# Revit family: Electronics_Amplifiers_Biamp_Tesira_4-Channel-PoE_AMP-450P__
name_source: partatom
category: Communication Devices
units: mm (PartAtom-declared; Revit-internal decimal feet)

## family parameters
Cut with Voids When Loaded = Yes
Host = Face
Maintain Annotation Orientation = No
OmniClass Number = 23.85.10.11.14.14.17
OmniClass Title = Sound Amplifiers
Part Type = Normal
Room Calculation Point = No
Round Connector Dimension = Use Diameter
Shared = No

## types (1)
- AMP-450P
    Altitude = 0-10,000 ft (0-3000m) MSL
    Amplifier Topology = Class D
    Apparent Load = 0 VA
    Burst Power Output = 4 ohm per channel: 50W per ANSI/CTA-2006-B at 1kHz; 8 ohm per channel: 30W per ANSI/CTA-2006-B at 1kHz
    Compliance = FCC Part 15B (USA); UL and C-UL listed (USA and Canada); CE Marked (Europe); KCC (Korea); RoHS Directive (Europe); Evaluated to the requirements of UL 2043 and is suitable for use in air handling spaces
    Connector Description = RJ-45; PoE+ (IEEE 802.3at Class 4 , 30W)
    Connectors = 4-pin 5.08 mm Phoenix connectors
    Continuous Power Output = Single Channel Driven 4 ohm, 8 ohm: 15W; Dual Channel Driven 4 ohm, 8 ohm: 7W; Four Channel Driven 4 ohm, 8 ohm: 3W
    Cooling = Convection
    Cross Talk = Channel to channel at 1kHz: < -90dB
    Default Elevation = 4' - 0"
    Depth = 0' - 4 11/16"
    Description = Tesira® AMP-450P 4-Channel PoE+ Conferencing Amplifier
    Dynamic Range = 20Hz-20kHz BW: > 90dB
    Frequency Response = 20Hz-20kHz: ± 1dB
    Height = 0' - 1 5/16"
    Housing Material = Biamp - Metal - Black
    Humidity = 0-95% relative humidity (non-condensing)
    Indicators = Power Indicator  (Green/Yellow/Red LED) Amp Status Indicator (Green/Yellow/Red LED)
    Intermodulation distortion = SMPTE: <0.3%
    Manufacturer = Biamp
    Max Power Consumption = 0 W
    Minimum Operational Load = 4 ohm
    Model = Tesira AMP-450P
    Network Connection = RJ-45 with Ethernet cable (Cat 5e and above)
    Number of Channels = 4
    Number of Poles = 1
    Power Factor = 1
    Product Documentation Link = https://downloads.biamp.com
    Product Page URL = https://www.biamp.com
    Product data url = https://www.bimobject.com
    THD+N = 20Hz-20kHz, at continuous power: < 0.3%
    Temperature Range = 32 - 104° F (0 - 40° C)
    URL = https://www.biamp.com
    Voltage = 0 V
    Weight = 1.50 lbf
    Width = 0' - 7 11/16"

## geometry (parser evidence)
native form markers: Sweep x2
no freeform markers — native parametric forms only
